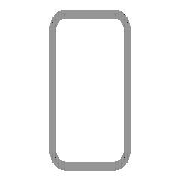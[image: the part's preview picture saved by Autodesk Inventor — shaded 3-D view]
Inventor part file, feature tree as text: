
AUTODESK INVENTOR PART (.ipt)
format: ipt  version: 2025 (Build 290162010, 162A)  size: 129,024 bytes
history: native  units: mm (DEFAULTED — no unit token found)
features: other x3, sketch x1, plane x1
ambient origin geometry x8: Origin, YZ Plane, XZ Plane, XY Plane, X Axis, Y Axis, Z Axis, Center Point
bodies: Solid1 (feature_tree), Body (feature_tree)
feature tree (5):
  other  "Driven Length"
  other  "Start plane"
  other  "End plane"
  sketch  "Sketch3"  dims[d3=1500.0mm d4=0.0mm d7=4.0mm d9=40.0mm d11=80.0mm d12=2.0mm d13=-0.0mm d14=1500.0mm d15=20.0mm d16=40.0mm d17=90.0deg d18=1500.0mm]
  plane  "Work Plane3"
